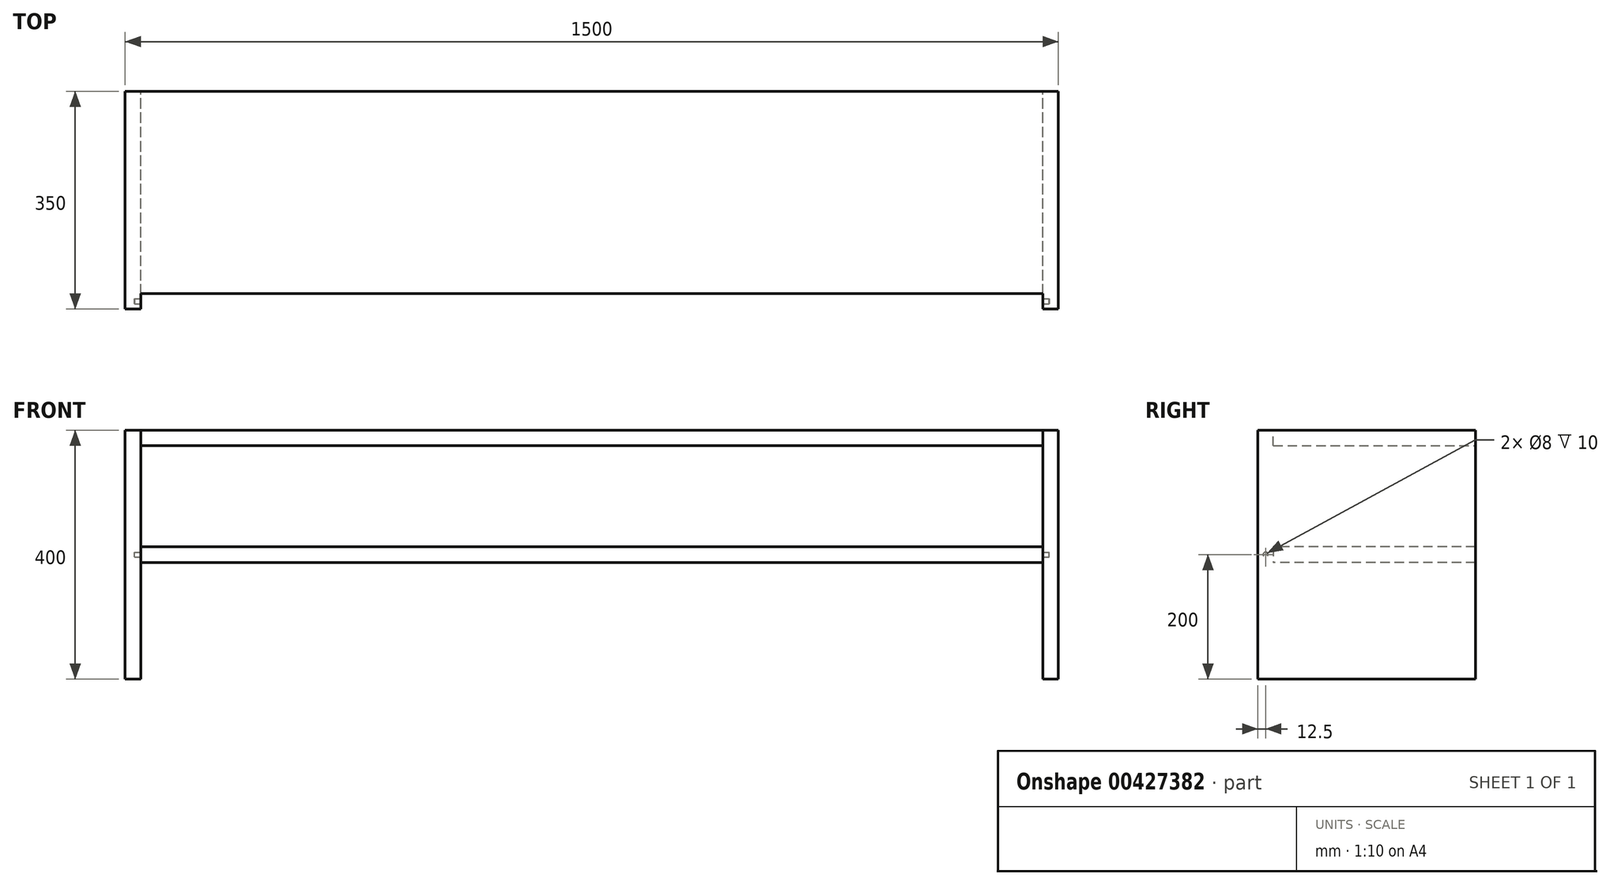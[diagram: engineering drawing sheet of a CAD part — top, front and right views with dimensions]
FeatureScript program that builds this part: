
annotation { "Feature Type Name" : "Feature", "Feature Type Description" : "" }
export const myFeature = defineFeature(function(context is Context, id is Id, definition is map)
    precondition{}
    {
        {
            var Q0;
            Q0=qCreatedBy(makeId("Top.planeOp"),FACE);
            var sketch = newSketch(context, id + "F0", { "sketchPlane" : qUnion([Q0])});
            skLineSegment(sketch, "E0.bottom", {"start": v(-750, 175) * mm, "end": v(750, 175) * mm});
            skLineSegment(sketch, "E0.top", {"start": v(-750, -175) * mm, "end": v(750, -175) * mm});
            skLineSegment(sketch, "E0.left", {"start": v(-750, 175) * mm, "end": v(-750, -175) * mm});
            skLineSegment(sketch, "E0.right", {"start": v(750, 175) * mm, "end": v(750, -175) * mm});
            skPoint(sketch, "E0.middle", {"position": v(0, 0) * mm});
            skSolve(sketch);
        }
        {
            var Q0;
            Q0=makeQuery(id+"F0.imprint","IMPRINT",FACE,{"disambiguationData":[TD([[makeQuery(id+"F0.imprint","IMPRINT",EDGE,{"derivedFrom":sQuery(id+"F0.wireOp",EDGE,"E0.bottom")}),-1.0]])]});
            extrude(context, id + "F1", {"entities" : qUnion([Q0]), "depth" : 25 * mm});
        }
        {
            var Q0;
            Q0=makeQuery(id+"F1.opExtrude","CAP_FACE",FACE,{"disambiguationData":[OSD([sQuery(id+"F0.wireOp",EDGE,"E0.bottom"),sQuery(id+"F0.wireOp",EDGE,"E0.top"),sQuery(id+"F0.wireOp",EDGE,"E0.left"),sQuery(id+"F0.wireOp",EDGE,"E0.right")])],"isStart":true});
            var sketch = newSketch(context, id + "F2", { "sketchPlane" : qUnion([Q0])});
            skLineSegment(sketch, "E1.bottom", {"start": v(-750, 175) * mm, "end": v(-725, 175) * mm});
            skLineSegment(sketch, "E1.top", {"start": v(-750, -175) * mm, "end": v(-725, -175) * mm});
            skLineSegment(sketch, "E1.left", {"start": v(-750, 175) * mm, "end": v(-750, -175) * mm});
            skLineSegment(sketch, "E1.right", {"start": v(-725, 175) * mm, "end": v(-725, -175) * mm});
            skLineSegment(sketch, "E2.bottom", {"start": v(750, 175) * mm, "end": v(725, 175) * mm});
            skLineSegment(sketch, "E2.top", {"start": v(750, -175) * mm, "end": v(725, -175) * mm});
            skLineSegment(sketch, "E2.left", {"start": v(750, 175) * mm, "end": v(750, -175) * mm});
            skLineSegment(sketch, "E2.right", {"start": v(725, 175) * mm, "end": v(725, -175) * mm});
            skSolve(sketch);
        }
        {
            var Q0;
            Q0 = qSketchRegion(id + "F2", true);
            extrude(context, id + "F3", {"entities" : qUnion([Q0]), "operationType" : NewBodyOperationType.ADD, "depth" : (400 - 25) * mm});
        }
        {
            var Q0;
            Q0=makeQuery(id+"F3.opExtrude","SWEPT_FACE",FACE,{"disambiguationData":[OSD([sQuery(id+"F2.wireOp",EDGE,"E1.right")])]});
            var sketch = newSketch(context, id + "F4", { "sketchPlane" : qUnion([Q0])});
            skLineSegment(sketch, "E3.bottom", {"start": v(175, -162.5) * mm, "end": v(-150, -162.5) * mm});
            skLineSegment(sketch, "E3.top", {"start": v(175, -187.5) * mm, "end": v(-150, -187.5) * mm});
            skLineSegment(sketch, "E3.left", {"start": v(175, -162.5) * mm, "end": v(175, -187.5) * mm});
            skLineSegment(sketch, "E3.right", {"start": v(-150, -162.5) * mm, "end": v(-150, -187.5) * mm});
            skSolve(sketch);
        }
        {
            var Q0;
            Q0 = qSketchRegion(id + "F4", true);
            var Q1;
            Q1=makeQuery(id+"F3.opExtrude","SWEPT_FACE",FACE,{"disambiguationData":[OSD([sQuery(id+"F2.wireOp",EDGE,"E2.right")])]});
            extrude(context, id + "F5", {"entities" : qUnion([Q0]), "operationType" : NewBodyOperationType.ADD, "endBound" : BoundingType.UP_TO_SURFACE, "endBoundEntityFace" : qUnion([Q1]), "depth" : 25 * mm});
        }
        {
            var Q0;
            Q0=qCreatedBy(makeId("Right.planeOp"),FACE);
            var sketch = newSketch(context, id + "F6", { "sketchPlane" : qUnion([Q0])});
            skCircle(sketch, "E4", {"center": v(-162.5, -175) * mm, "radius": 4 * mm});
            skSolve(sketch);
        }
        {
            var Q0;
            Q0 = qSketchRegion(id + "F6", true);
            extrude(context, id + "F7", {"entities" : qUnion([Q0]), "operationType" : NewBodyOperationType.REMOVE, "endBound" : BoundingType.SYMMETRIC, "oppositeDirection" : true, "depth" : 1470 * mm});
        }
        {
            var Q0;
            Q0=makeQuery(id+"F1.opExtrude","CAP_FACE",FACE,{"disambiguationData":[OSD([sQuery(id+"F0.wireOp",EDGE,"E0.bottom"),sQuery(id+"F0.wireOp",EDGE,"E0.top"),sQuery(id+"F0.wireOp",EDGE,"E0.left"),sQuery(id+"F0.wireOp",EDGE,"E0.right")])],"isStart":false});
            var sketch = newSketch(context, id + "F8", { "sketchPlane" : qUnion([Q0])});
            skLineSegment(sketch, "E5.bottom", {"start": v(-725, -175) * mm, "end": v(725, -175) * mm});
            skLineSegment(sketch, "E5.top", {"start": v(-725, -150) * mm, "end": v(725, -150) * mm});
            skLineSegment(sketch, "E5.left", {"start": v(-725, -175) * mm, "end": v(-725, -150) * mm});
            skLineSegment(sketch, "E5.right", {"start": v(725, -175) * mm, "end": v(725, -150) * mm});
            skSolve(sketch);
        }
        {
            var Q0;
            Q0 = qSketchRegion(id + "F8", true);
            extrude(context, id + "F9", {"entities" : qUnion([Q0]), "operationType" : NewBodyOperationType.REMOVE, "oppositeDirection" : true, "depth" : 25 * mm});
        }
    });
